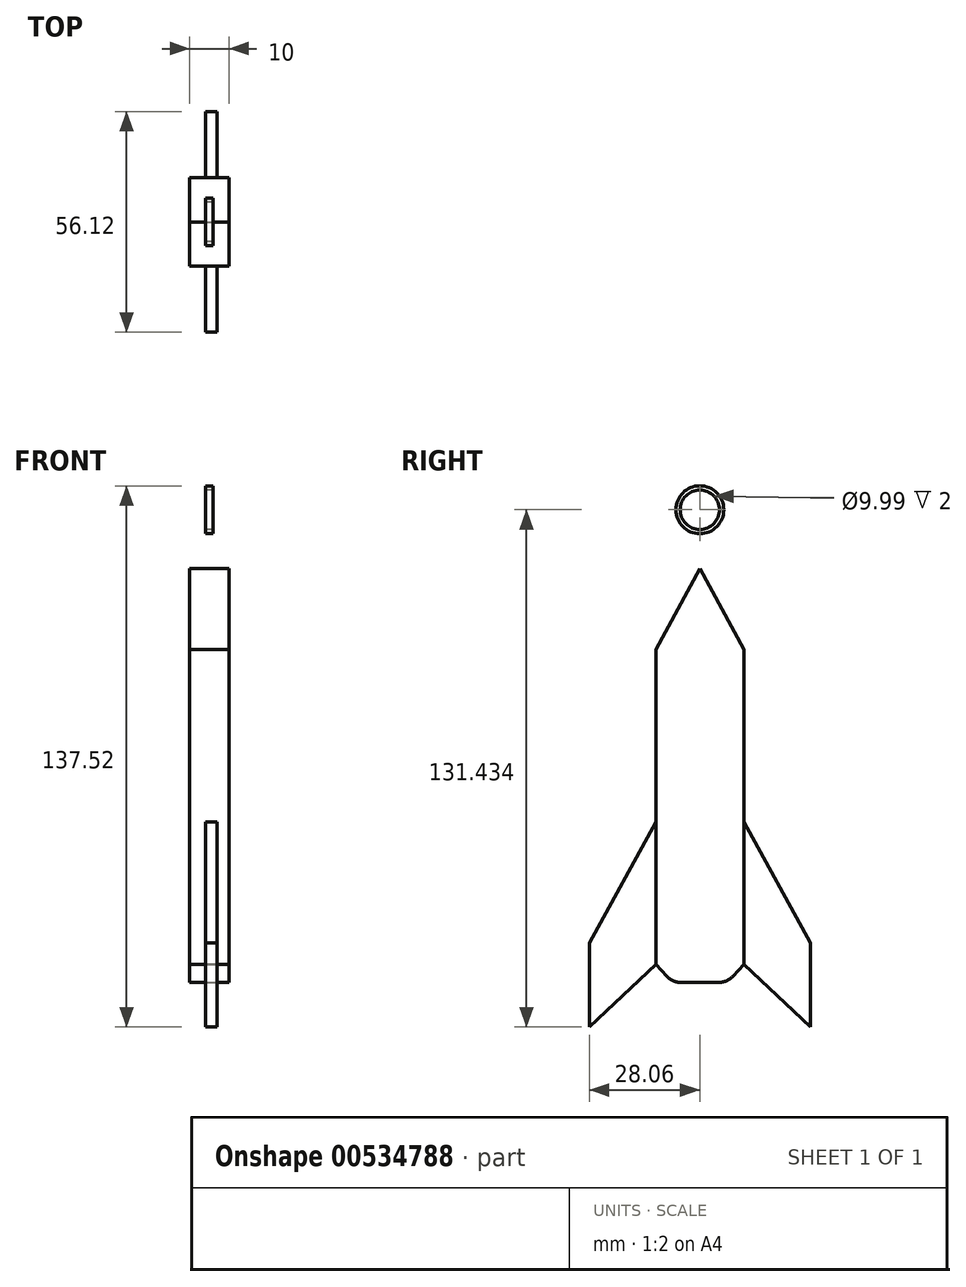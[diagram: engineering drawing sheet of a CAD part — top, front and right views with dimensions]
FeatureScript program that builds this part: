
annotation { "Feature Type Name" : "Feature", "Feature Type Description" : "" }
export const myFeature = defineFeature(function(context is Context, id is Id, definition is map)
    precondition{}
    {
        {
            var Q0;
            Q0=qCreatedBy(makeId("Right.planeOp"),FACE);
            var sketch = newSketch(context, id + "F0", { "sketchPlane" : qUnion([Q0])});
            skLineSegment(sketch, "E0", {"start": v(0, 58.84) * mm, "end": v(-11.2, 38.17) * mm});
            skLineSegment(sketch, "E1", {"start": v(-11.2, 38.17) * mm, "end": v(-11.2, -41.83) * mm});
            skLineSegment(sketch, "E2", {"start": v(0, 58.84) * mm, "end": v(11.2, 38.17) * mm});
            skLineSegment(sketch, "E3", {"start": v(11.2, 38.17) * mm, "end": v(11.2, -41.83) * mm});
            skLineSegment(sketch, "E4", {"start": v(-11.2, -41.83) * mm, "end": v(11.2, -41.83) * mm});
            skLineSegment(sketch, "E5", {"start": v(11.2, -5.59) * mm, "end": v(28.06, -36.35) * mm});
            skLineSegment(sketch, "E6", {"start": v(28.06, -36.35) * mm, "end": v(28.06, -57.7) * mm});
            skLineSegment(sketch, "E7", {"start": v(28.06, -57.7) * mm, "end": v(11.2, -41.83) * mm});
            skLineSegment(sketch, "E8.MirrorCS", {"start": v(-11.2, -5.59) * mm, "end": v(-28.06, -36.35) * mm});
            skLineSegment(sketch, "E9.MirrorCS", {"start": v(-28.06, -36.35) * mm, "end": v(-28.06, -57.7) * mm});
            skLineSegment(sketch, "E10.MirrorCS", {"start": v(-28.06, -57.7) * mm, "end": v(-11.2, -41.83) * mm});
            skLineSegment(sketch, "E11", {"start": v(-28.06, -57.7) * mm, "end": v(-28.06, -66.49) * mm});
            skLineSegment(sketch, "E12.MirrorCS", {"start": v(28.06, -57.7) * mm, "end": v(28.06, -66.49) * mm});
            skLineSegment(sketch, "E13", {"start": v(-11.2, -41.83) * mm, "end": v(-8.4, -44.8) * mm});
            skLineSegment(sketch, "E14.MirrorCS", {"start": v(11.2, -41.83) * mm, "end": v(8.4, -44.8) * mm});
            skLineSegment(sketch, "E15", {"start": v(-4.75, -46.38) * mm, "end": v(4.75, -46.38) * mm});
            skLineSegment(sketch, "E16", {"start": v(0, 58.84) * mm, "end": v(0, 67.6) * mm});
            skCircle(sketch, "E17", {"center": v(0, 73.73) * mm, "radius": 6.09 * mm});
            skPoint(sketch, "E18.visualSharp", {"position": v(-6.91, -46.38) * mm});
            skArc(sketch, "E18.filletArc", {"start": v(-8.4, -44.8) * mm, "mid": v(-6.74, -45.97) * mm, "end": v(-4.75, -46.38) * mm});
            skPoint(sketch, "E19.visualSharp", {"position": v(6.91, -46.38) * mm});
            skArc(sketch, "E19.filletArc", {"start": v(4.75, -46.38) * mm, "mid": v(6.74, -45.97) * mm, "end": v(8.4, -44.8) * mm});
            skCircle(sketch, "E20", {"center": v(0, 73.73) * mm, "radius": 5 * mm});
            skSolve(sketch);
        }
        {
            var Q0;
            {var subQ4=sQuery(id+"F0.wireOp",EDGE,"E0");Q0=makeQuery(id+"F0.imprint","IMPRINT",FACE,{"disambiguationData":[TD([[makeQuery(id+"F0.imprint","IMPRINT",EDGE,{"derivedFrom":subQ4}),1.0]])]});}
            var Q1;
            Q1=makeQuery(id+"F0.imprint","IMPRINT",FACE,{"disambiguationData":[TD([[makeQuery(id+"F0.imprint","IMPRINT",EDGE,{"derivedFrom":sQuery(id+"F0.wireOp",EDGE,"E4")}),-1.0]])]});
            extrude(context, id + "F1", {"entities" : qUnion([Q0, Q1]), "oppositeDirection" : true, "depth" : 10 * mm, "offsetDistance" : 25 * mm});
        }
        {
            var Q0;
            {var subQ2=sQuery(id+"F0.wireOp",EDGE,"E5");Q0=makeQuery(id+"F0.imprint","IMPRINT",FACE,{"disambiguationData":[TD([[makeQuery(id+"F0.imprint","IMPRINT",EDGE,{"derivedFrom":subQ2}),-1.0]])]});}
            var Q1;
            {var subQ2=sQuery(id+"F0.wireOp",EDGE,"E8.MirrorCS");Q1=makeQuery(id+"F0.imprint","IMPRINT",FACE,{"disambiguationData":[TD([[makeQuery(id+"F0.imprint","IMPRINT",EDGE,{"derivedFrom":subQ2}),1.0]])]});}
            extrude(context, id + "F2", {"entities" : qUnion([Q0, Q1]), "depth" : 3 * mm, "offsetDistance" : 25 * mm});
        }
        {
            var Q0;
            Q0=makeQuery(id+"F0.imprint","IMPRINT",FACE,{"disambiguationData":[TD([[makeQuery(id+"F0.imprint","IMPRINT",EDGE,{"derivedFrom":sQuery(id+"F0.wireOp",EDGE,"E17")}),1.0]])]});
            extrude(context, id + "F3", {"entities" : qUnion([Q0]), "depth" : 2 * mm, "offsetDistance" : 25 * mm});
        }
        {
            var Q0;
            Q0=sQuery(id+"F0.wireOp",EDGE,"E16");
            extrude(context, id + "F4", {"bodyType" : ToolBodyType.SURFACE, "surfaceEntities" : qUnion([Q0]), "depth" : 2 * mm, "offsetDistance" : 25 * mm});
        }
        {
            var Q0;
            Q0=makeQuery(id+"F2.opExtrude","SWEPT_BODY",BODY,{"disambiguationData":[OSD([sQuery(id+"F0.wireOp",EDGE,"E3"),sQuery(id+"F0.wireOp",EDGE,"E5"),sQuery(id+"F0.wireOp",EDGE,"E6"),sQuery(id+"F0.wireOp",EDGE,"E7")])]});
            transform(context, id + "F5", {"entities" : qUnion([Q0]), "transformType" : TransformType.TRANSLATION_3D, "dx" : -6 * mm, "dy" : 0 * mm, "dz" : 0 * mm, "makeCopy" : false});
        }
        {
            var Q0;
            Q0=makeQuery(id+"F2.opExtrude","SWEPT_BODY",BODY,{"disambiguationData":[OSD([sQuery(id+"F0.wireOp",EDGE,"E1"),sQuery(id+"F0.wireOp",EDGE,"E8.MirrorCS"),sQuery(id+"F0.wireOp",EDGE,"E9.MirrorCS"),sQuery(id+"F0.wireOp",EDGE,"E10.MirrorCS")])]});
            transform(context, id + "F6", {"entities" : qUnion([Q0]), "transformType" : TransformType.TRANSLATION_3D, "dx" : -6 * mm, "dy" : 0 * mm, "dz" : 0 * mm, "makeCopy" : false});
        }
        {
            var Q0;
            Q0=makeQuery(id+"F3.opExtrude","SWEPT_BODY",BODY,{"disambiguationData":[OSD([sQuery(id+"F0.wireOp",EDGE,"E17")])]});
            transform(context, id + "F7", {"entities" : qUnion([Q0]), "transformType" : TransformType.TRANSLATION_3D, "dx" : -6 * mm, "dy" : 0 * mm, "dz" : 0 * mm, "makeCopy" : false});
        }
        {
            var Q0;
            Q0=makeQuery(id+"F4.opExtrude","SWEPT_BODY",BODY,{"disambiguationData":[OSD([sQuery(id+"F0.wireOp",EDGE,"E16")])]});
            transform(context, id + "F8", {"entities" : qUnion([Q0]), "transformType" : TransformType.TRANSLATION_3D, "dx" : -6 * mm, "dy" : 0 * mm, "dz" : 0 * mm, "makeCopy" : false});
        }
    });
